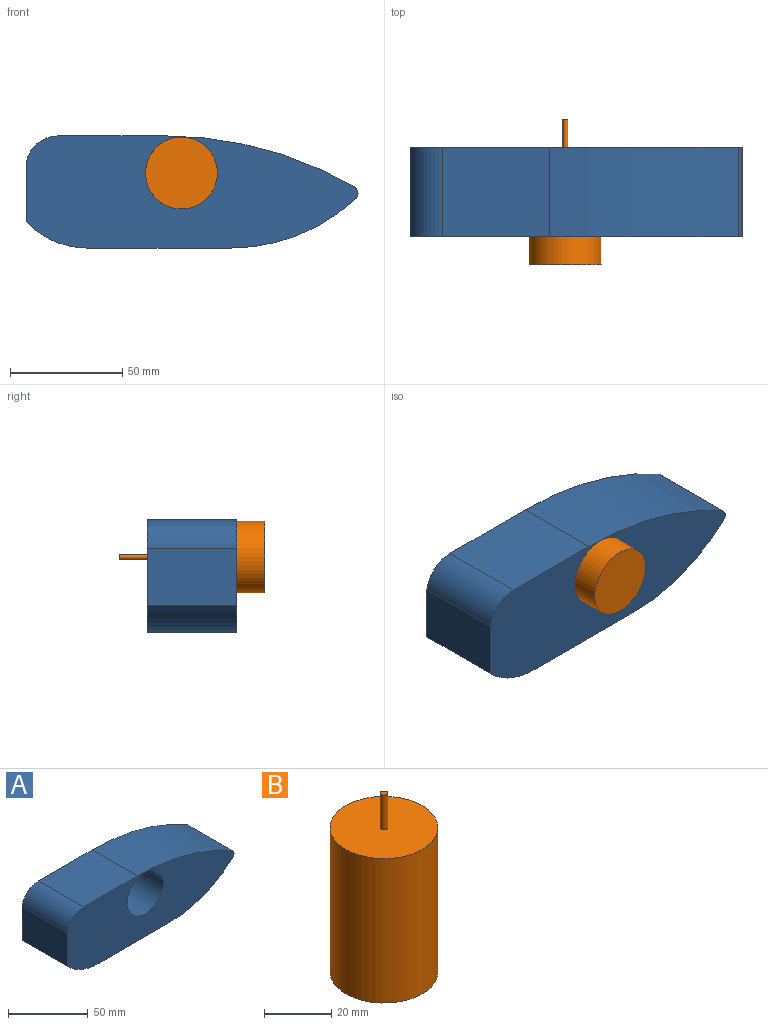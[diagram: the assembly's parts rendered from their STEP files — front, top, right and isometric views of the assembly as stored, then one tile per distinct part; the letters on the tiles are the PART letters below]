
ASSEMBLY  parts=2 mates=1
PART A: 11 faces, bbox 147.9x40x50 mm
  f0: cylinder r=38.18mm len=40mm, axis (0,1,0), area 1230.3mm2, adj f1,f7,f8,f9
  f1: plane 63.42x40mm, normal (0,0,-1), area 2537mm2, adj f0,f2,f8,f9
  f2: cylinder r=82.21mm len=55.86mm, axis (0,1,0), area 2456.7mm2, adj f1,f8,f9,f10
  f3: cylinder r=167.02mm len=84.13mm, axis (0,1,0), area 3526.7mm2, adj f4,f8,f9,f10
  f4: plane 47.66x40mm, normal (0,0,1), area 1906.4mm2, adj f3,f5,f8,f9
  f5: cylinder r=14.58mm len=40mm, axis (0,1,0), area 836.7mm2, adj f4,f7,f8,f9
  f6: cylinder r=16mm len=40mm, axis (0,1,0), area 4021.2mm2, adj f8,f9
  f7: plane 40x25.66mm, normal (-1,0,0), area 1026.6mm2, adj f0,f5,f8,f9
  f8: plane 147.9x50mm, normal (0,-1,0), area 5380.8mm2, adj f0,f1,f2,f3,f4,f5,f6,f7
  f9: plane 147.9x50mm, normal (0,1,0), area 5380.8mm2, adj f0,f1,f2,f3,f4,f5,f6,f7
  f10: cylinder r=3.36mm len=40mm, axis (0,1,0), area 251mm2, adj f2,f3,f8,f9
PART B: 5 faces, bbox 32x32x65 mm
  f0: plane 32x32mm, normal (0,0,-1), area 804.2mm2, adj f1
  f1: cylinder r=16mm len=52.5mm, axis (0,0,-1), area 5277.9mm2, adj f0,f2
  f2: plane 32x32mm, normal (0,0,1), area 800.4mm2, adj f1,f3
  f3: cylinder r=1.1mm len=12.5mm, axis (0,0,-1), area 86.4mm2, adj f2,f4
  f4: plane 2.2x2.2mm, normal (0,0,1), area 3.8mm2, adj f3
PLACE A t=(0.04,122.23,-0.15)mm
PLACE B rot(axis=(-1,0,0),90deg) t=(69.28,69.73,33.3)mm
MATE fastened A.f6 <-> B.f1  axis (0,1,0) through (69.28,122.23,33.3)mm
